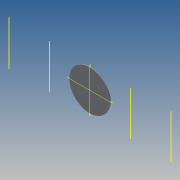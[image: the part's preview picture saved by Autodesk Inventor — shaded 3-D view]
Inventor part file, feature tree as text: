
AUTODESK INVENTOR PART (.ipt)
format: ipt  version: 2017.3 (Build 213257000, 257)  size: 211,456 bytes
history: native  units: in
note: dims shown in document units (in); Inventor stores cm internally (conversion verified against a paired STEP export)
features: other x13, extrude x3, sketch x2, split x2, hole x1
ambient origin geometry x8: Origin, YZ Plane, XZ Plane, XY Plane, X Axis, Y Axis, Z Axis, Center Point
bodies: Solid1 (feature_tree), Solid2 (feature_tree), Solid3 (feature_tree)
feature tree (21):
  other  "Centerline at Trunk OD"
  other  "Centerline at Repad OD"
  other  "Offset at Repad OD"
  other  "Bottom quadrant line - right"
  other  "Right quadrant line"
  other  "Bottom quadrant line - left"
  other  "Left quadrant line"
  other  "Top quadrant line"
  other  "Centerline at centerline"
  sketch  "Sketch1"  dims[d0=-0.0in d1=-0.0in]
  extrude  "Extrusion1"  [1 undecoded]
  split  "Split1"
  split  "Split2"
  hole  "Hole1"  [1 undecoded]
  other  "2D Equation Curve1"
  other  "2D Equation Curve2"
  other  "Srf1"
  other  "Srf2"
  sketch  "Sketch3"  dims[d2=0.0in d3=54.9779in d4=27.4889in d5=-54.9779in d6=-27.4889in d7=0.0in d8=0.0in d9=0.0in d10=141.7323in d11=0.0in d12=141.7323in d14=7.5in d15=7.5in d25=5.5in d26=0.5in d27=0.0in d28=0.5in d29=0.0in d30=0.5in d31=0.0in d32=6.0in d36=0.422in d37=0.339in d38=0.0246in d39=0.426in d40=0.375in d41=0.25in d42=0.5635in d43=1.0in d44=0.8108in d45=12.0in]
  extrude  "ExtrusionSrf1"  Depth=27.4889in
  extrude  "ExtrusionSrf2"  [1 undecoded]
note: 3 required parameter values undecoded (feature->parameter linkage not recoverable at this tier; creation-order binding heuristic only, values carry confidence <= 0.55)
